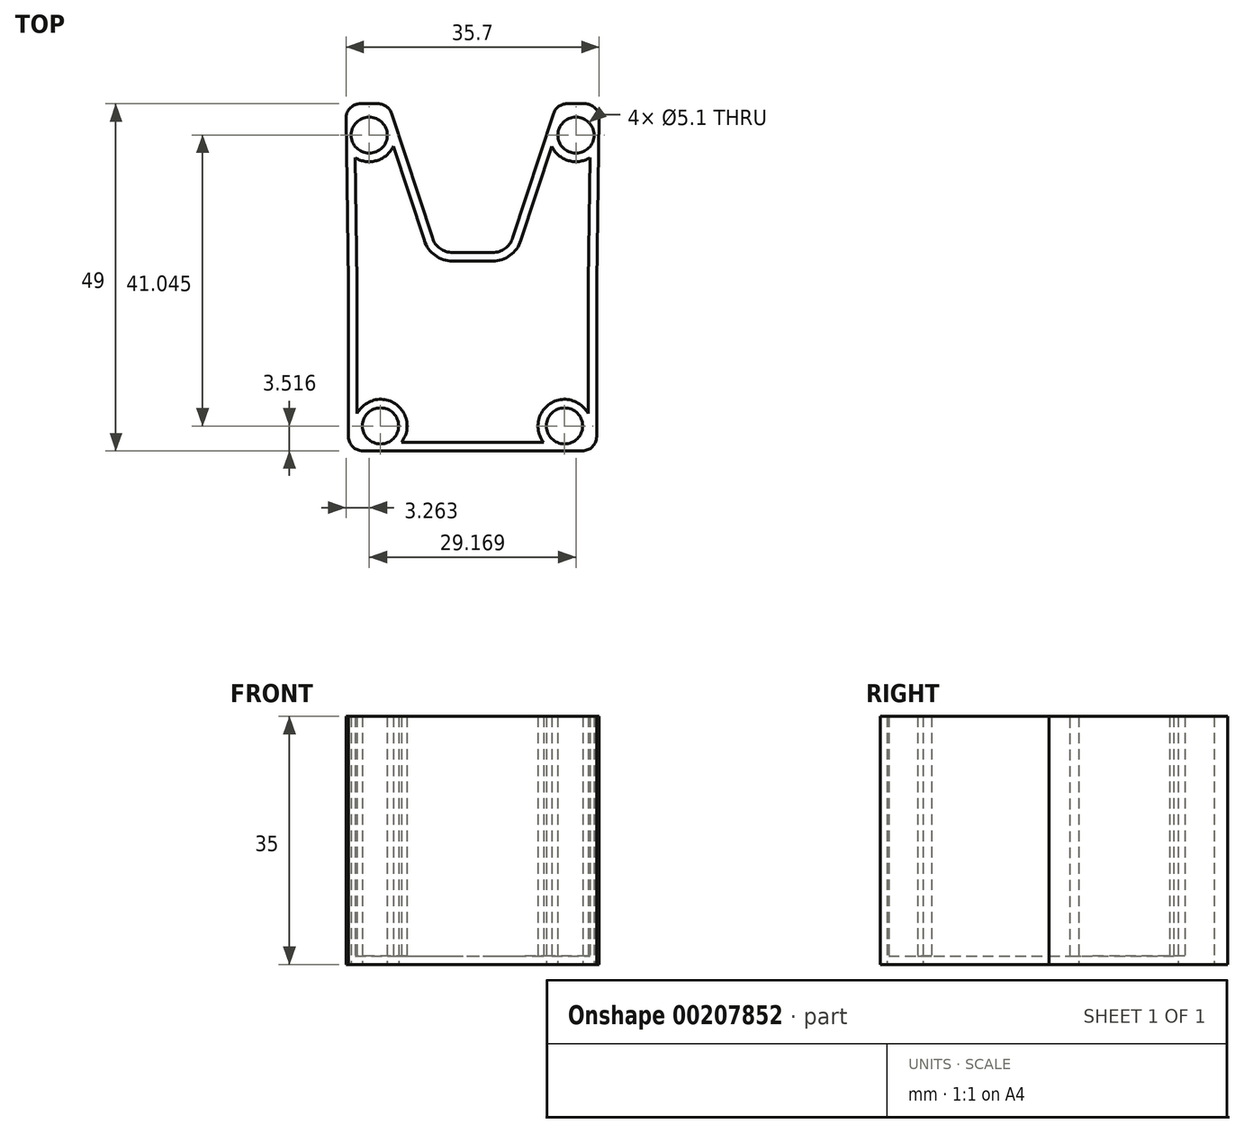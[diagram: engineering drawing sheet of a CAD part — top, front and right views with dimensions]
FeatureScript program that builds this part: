
annotation { "Feature Type Name" : "Feature", "Feature Type Description" : "" }
export const myFeature = defineFeature(function(context is Context, id is Id, definition is map)
    precondition{}
    {
        {
            var Q0;
            Q0=qCreatedBy(makeId("Top.planeOp"),FACE);
            var sketch = newSketch(context, id + "F0", { "sketchPlane" : qUnion([Q0])});
            skLineSegment(sketch, "E0.bottom", {"start": v(12.57, -4.38) * mm, "end": v(30.07, -4.38) * mm});
            skLineSegment(sketch, "E0.right", {"start": v(30.07, -2.38) * mm, "end": v(30.07, 19.44) * mm});
            skLineSegment(sketch, "E1", {"start": v(12.57, -4.38) * mm, "end": v(12.57, 23.62) * mm});
            skLineSegment(sketch, "E2", {"start": v(12.57, 23.62) * mm, "end": v(17.57, 23.62) * mm});
            skLineSegment(sketch, "E3", {"start": v(15.4, 23.62) * mm, "end": v(12.57, 23.62) * mm});
            skLineSegment(sketch, "E4.top", {"start": v(12.57, -4.38) * mm, "end": v(28.07, -4.38) * mm});
            skLineSegment(sketch, "E5", {"start": v(30.07, 19.44) * mm, "end": v(30.42, 42.59) * mm});
            skLineSegment(sketch, "E6", {"start": v(28.42, 44.62) * mm, "end": v(25.9, 44.62) * mm});
            skLineSegment(sketch, "E7", {"start": v(24, 43.24) * mm, "end": v(18.24, 25.68) * mm});
            skLineSegment(sketch, "E8.trimOffspring", {"start": v(24.45, 44.62) * mm, "end": v(30.45, 44.62) * mm});
            skLineSegment(sketch, "E9.trimOffspring", {"start": v(24.45, 44.62) * mm, "end": v(30.07, 44.62) * mm});
            skPoint(sketch, "E10.visualSharp", {"position": v(30.45, 44.62) * mm});
            skArc(sketch, "E10.filletArc", {"start": v(30.42, 42.59) * mm, "mid": v(29.84, 44.02) * mm, "end": v(28.42, 44.62) * mm});
            skPoint(sketch, "E11.visualSharp", {"position": v(24.45, 44.62) * mm});
            skArc(sketch, "E11.filletArc", {"start": v(25.9, 44.62) * mm, "mid": v(24.72, 44.24) * mm, "end": v(24, 43.24) * mm});
            skPoint(sketch, "E12.visualSharp", {"position": v(17.57, 23.62) * mm});
            skArc(sketch, "E12.filletArc", {"start": v(15.4, 23.62) * mm, "mid": v(17.15, 24.19) * mm, "end": v(18.24, 25.68) * mm});
            skArc(sketch, "E13.MirrorCS", {"start": v(-0.76, 44.62) * mm, "mid": v(0.4, 44.24) * mm, "end": v(1.14, 43.24) * mm});
            skLineSegment(sketch, "E14.MirrorCS", {"start": v(-3.28, 44.62) * mm, "end": v(-0.76, 44.62) * mm});
            skArc(sketch, "E15.MirrorCS", {"start": v(9.74, 23.62) * mm, "mid": v(7.98, 24.19) * mm, "end": v(6.9, 25.68) * mm});
            skLineSegment(sketch, "E16.MirrorCS", {"start": v(9.74, 23.62) * mm, "end": v(12.57, 23.62) * mm});
            skLineSegment(sketch, "E17.MirrorCS", {"start": v(12.57, 23.62) * mm, "end": v(7.57, 23.62) * mm});
            skLineSegment(sketch, "E18.MirrorCS", {"start": v(0.69, 44.62) * mm, "end": v(-5.31, 44.62) * mm});
            skLineSegment(sketch, "E19.MirrorCS", {"start": v(0.69, 44.62) * mm, "end": v(-4.93, 44.62) * mm});
            skArc(sketch, "E20.MirrorCS", {"start": v(-5.28, 42.59) * mm, "mid": v(-4.7, 44.02) * mm, "end": v(-3.28, 44.62) * mm});
            skLineSegment(sketch, "E21.MirrorCS", {"start": v(12.57, -4.38) * mm, "end": v(-2.93, -4.38) * mm});
            skPoint(sketch, "E22.MirrorP", {"position": v(-5.31, 44.62) * mm});
            skLineSegment(sketch, "E23.MirrorCS", {"start": v(1.14, 43.24) * mm, "end": v(6.9, 25.68) * mm});
            skPoint(sketch, "E24.MirrorP", {"position": v(7.57, 23.62) * mm});
            skLineSegment(sketch, "E25.MirrorCS", {"start": v(-4.93, 19.44) * mm, "end": v(-5.28, 42.59) * mm});
            skLineSegment(sketch, "E26.MirrorCS", {"start": v(-4.93, -2.38) * mm, "end": v(-4.93, 19.44) * mm});
            skPoint(sketch, "E27.MirrorP", {"position": v(0.69, 44.62) * mm});
            skPoint(sketch, "E28.orphan", {"position": v(-8.52, -4.38) * mm});
            skPoint(sketch, "E29.orphan", {"position": v(33.65, -4.38) * mm});
            skPoint(sketch, "E30.visualSharp", {"position": v(-4.93, -4.38) * mm});
            skArc(sketch, "E30.filletArc", {"start": v(-4.93, -2.38) * mm, "mid": v(-4.35, -3.8) * mm, "end": v(-2.93, -4.38) * mm});
            skPoint(sketch, "E31.visualSharp", {"position": v(30.07, -4.38) * mm});
            skArc(sketch, "E31.filletArc", {"start": v(28.07, -4.38) * mm, "mid": v(29.48, -3.8) * mm, "end": v(30.07, -2.38) * mm});
            skLineSegment(sketch, "E32", {"start": v(-4.93, -2.38) * mm, "end": v(-1.93, -2.38) * mm});
            skLineSegment(sketch, "E33", {"start": v(-1.93, -2.38) * mm, "end": v(-1.93, -4.38) * mm});
            skCircle(sketch, "E34", {"center": v(-0.42, -0.86) * mm, "radius": 1.5 * mm});
            skLineSegment(sketch, "E35", {"start": v(-1.93, -2.38) * mm, "end": v(-1.93, 2.04) * mm});
            skLineSegment(sketch, "E36", {"start": v(-1.93, -2.38) * mm, "end": v(2.26, -2.38) * mm});
            skLineSegment(sketch, "E37.MirrorCS", {"start": v(27.07, -2.38) * mm, "end": v(27.07, -4.38) * mm});
            skLineSegment(sketch, "E38.MirrorCS", {"start": v(30.07, -2.38) * mm, "end": v(27.07, -2.38) * mm});
            skLineSegment(sketch, "E39.MirrorCS", {"start": v(27.07, -2.38) * mm, "end": v(22.87, -2.38) * mm});
            skLineSegment(sketch, "E40.MirrorCS", {"start": v(27.07, -2.38) * mm, "end": v(27.07, 2.04) * mm});
            skCircle(sketch, "E41.MirrorC", {"center": v(25.55, -0.86) * mm, "radius": 1.5 * mm});
            skLineSegment(sketch, "E42", {"start": v(-3.28, 44.62) * mm, "end": v(-3.28, 42.62) * mm});
            skLineSegment(sketch, "E43", {"start": v(-5.28, 42.59) * mm, "end": v(-3.28, 42.62) * mm});
            skLineSegment(sketch, "E44", {"start": v(-2.02, 44.62) * mm, "end": v(-2.02, 40.12) * mm});
            skCircle(sketch, "E45", {"center": v(-2.02, 40.18) * mm, "radius": 1.5 * mm});
            skCircle(sketch, "E46.MirrorC", {"center": v(27.15, 40.18) * mm, "radius": 1.5 * mm});
            skLineSegment(sketch, "E47.bottom", {"start": v(20, 2.29) * mm, "end": v(5.14, 2.29) * mm});
            skLineSegment(sketch, "E47.top", {"start": v(20, 13.23) * mm, "end": v(5.14, 13.23) * mm});
            skLineSegment(sketch, "E47.left", {"start": v(20, 2.29) * mm, "end": v(20, 13.23) * mm});
            skLineSegment(sketch, "E47.right", {"start": v(5.14, 2.29) * mm, "end": v(5.14, 13.23) * mm});
            skPoint(sketch, "E47.middle", {"position": v(12.57, 7.76) * mm});
            skLineSegment(sketch, "E48.bottom", {"start": v(28.44, 3.6) * mm, "end": v(-3.3, 3.6) * mm});
            skLineSegment(sketch, "E48.top", {"start": v(28.44, 6.21) * mm, "end": v(-3.3, 6.21) * mm});
            skLineSegment(sketch, "E48.left", {"start": v(28.44, 3.6) * mm, "end": v(28.44, 6.21) * mm});
            skLineSegment(sketch, "E48.right", {"start": v(-3.3, 3.6) * mm, "end": v(-3.3, 6.21) * mm});
            skPoint(sketch, "E48.middle", {"position": v(12.57, 4.9) * mm});
            skCircle(sketch, "E49", {"center": v(-2.02, 40.18) * mm, "radius": 2.55 * mm});
            skCircle(sketch, "E50", {"center": v(27.15, 40.18) * mm, "radius": 2.55 * mm});
            skCircle(sketch, "E51", {"center": v(25.55, -0.86) * mm, "radius": 2.55 * mm});
            skCircle(sketch, "E52", {"center": v(-0.42, -0.86) * mm, "radius": 2.55 * mm});
            skSolve(sketch);
        }
        {
            var Q0;
            Q0 = qSketchRegion(id + "F0", true);
            var Q1;
            {var subQ0=sQuery(id+"F0.wireOp",EDGE,"E48.top");var subQ1=sQuery(id+"F0.wireOp",EDGE,"E1");var subQ2=makeQuery(id+"F0.imprint","INTERSECT",VERTEX,{"derivedFrom":[subQ1,subQ0]});Q1=makeQuery(id+"F0.imprint","IMPRINT",FACE,{"disambiguationData":[TD([[makeQuery(id+"F0.imprint","IMPRINT",EDGE,{"disambiguationData":[TD([[subQ2,-1.0]])],"derivedFrom":subQ1}),1.0]])]});}
            var Q2;
            {var subQ0=sQuery(id+"F0.wireOp",EDGE,"E48.top");var subQ1=sQuery(id+"F0.wireOp",EDGE,"E1");var subQ2=makeQuery(id+"F0.imprint","INTERSECT",VERTEX,{"derivedFrom":[subQ1,subQ0]});Q2=makeQuery(id+"F0.imprint","IMPRINT",FACE,{"disambiguationData":[TD([[makeQuery(id+"F0.imprint","IMPRINT",EDGE,{"disambiguationData":[TD([[subQ2,-1.0]])],"derivedFrom":subQ1}),-1.0]])]});}
            var Q3;
            {var subQ5=sQuery(id+"F0.wireOp",EDGE,"E48.left");Q3=makeQuery(id+"F0.imprint","IMPRINT",FACE,{"disambiguationData":[TD([[makeQuery(id+"F0.imprint","IMPRINT",EDGE,{"derivedFrom":subQ5}),1.0]])]});}
            var Q4;
            {var subQ0=sQuery(id+"F0.wireOp",EDGE,"E48.bottom");var subQ1=sQuery(id+"F0.wireOp",EDGE,"E1");var subQ2=makeQuery(id+"F0.imprint","INTERSECT",VERTEX,{"derivedFrom":[subQ1,subQ0]});Q4=makeQuery(id+"F0.imprint","IMPRINT",FACE,{"disambiguationData":[TD([[makeQuery(id+"F0.imprint","IMPRINT",EDGE,{"disambiguationData":[TD([[subQ2,-1.0]])],"derivedFrom":subQ1}),1.0]])]});}
            var Q5;
            {var subQ5=sQuery(id+"F0.wireOp",EDGE,"E48.right");Q5=makeQuery(id+"F0.imprint","IMPRINT",FACE,{"disambiguationData":[TD([[makeQuery(id+"F0.imprint","IMPRINT",EDGE,{"derivedFrom":subQ5}),-1.0]])]});}
            var Q6;
            {var subQ0=sQuery(id+"F0.wireOp",EDGE,"E47.bottom");var subQ1=sQuery(id+"F0.wireOp",EDGE,"E1");var subQ2=makeQuery(id+"F0.imprint","INTERSECT",VERTEX,{"derivedFrom":[subQ1,subQ0]});Q6=makeQuery(id+"F0.imprint","IMPRINT",FACE,{"disambiguationData":[TD([[makeQuery(id+"F0.imprint","IMPRINT",EDGE,{"disambiguationData":[TD([[subQ2,-1.0]])],"derivedFrom":subQ1}),1.0]])]});}
            var Q7;
            {var subQ0=sQuery(id+"F0.wireOp",EDGE,"E48.bottom");var subQ1=sQuery(id+"F0.wireOp",EDGE,"E1");var subQ2=makeQuery(id+"F0.imprint","INTERSECT",VERTEX,{"derivedFrom":[subQ1,subQ0]});Q7=makeQuery(id+"F0.imprint","IMPRINT",FACE,{"disambiguationData":[TD([[makeQuery(id+"F0.imprint","IMPRINT",EDGE,{"disambiguationData":[TD([[subQ2,-1.0]])],"derivedFrom":subQ1}),-1.0]])]});}
            var Q8;
            {var subQ0=sQuery(id+"F0.wireOp",EDGE,"E47.bottom");var subQ1=sQuery(id+"F0.wireOp",EDGE,"E1");var subQ2=makeQuery(id+"F0.imprint","INTERSECT",VERTEX,{"derivedFrom":[subQ1,subQ0]});Q8=makeQuery(id+"F0.imprint","IMPRINT",FACE,{"disambiguationData":[TD([[makeQuery(id+"F0.imprint","IMPRINT",EDGE,{"disambiguationData":[TD([[subQ2,-1.0]])],"derivedFrom":subQ1}),-1.0]])]});}
            extrude(context, id + "F1", {"entities" : qUnion([Q0, Q1, Q2, Q3, Q4, Q5, Q6, Q7, Q8]), "depth" : 35 * mm});
        }
        {
            var Q0;
            Q0=makeQuery(id+"F1.opExtrude","CAP_FACE",FACE,{"disambiguationData":[OSD([sQuery(id+"F0.wireOp",EDGE,"E0.right"),sQuery(id+"F0.wireOp",EDGE,"E3"),sQuery(id+"F0.wireOp",EDGE,"E4.top"),sQuery(id+"F0.wireOp",EDGE,"E5"),sQuery(id+"F0.wireOp",EDGE,"E7"),sQuery(id+"F0.wireOp",EDGE,"E9.trimOffspring"),sQuery(id+"F0.wireOp",EDGE,"E10.filletArc"),sQuery(id+"F0.wireOp",EDGE,"E11.filletArc"),sQuery(id+"F0.wireOp",EDGE,"E12.filletArc"),sQuery(id+"F0.wireOp",EDGE,"E13.MirrorCS"),sQuery(id+"F0.wireOp",EDGE,"E15.MirrorCS"),sQuery(id+"F0.wireOp",EDGE,"E17.MirrorCS"),sQuery(id+"F0.wireOp",EDGE,"E19.MirrorCS"),sQuery(id+"F0.wireOp",EDGE,"E20.MirrorCS"),sQuery(id+"F0.wireOp",EDGE,"E23.MirrorCS"),sQuery(id+"F0.wireOp",EDGE,"E25.MirrorCS"),sQuery(id+"F0.wireOp",EDGE,"E21.MirrorCS"),sQuery(id+"F0.wireOp",EDGE,"E26.MirrorCS"),sQuery(id+"F0.wireOp",EDGE,"E30.filletArc"),sQuery(id+"F0.wireOp",EDGE,"E31.filletArc"),sQuery(id+"F0.wireOp",EDGE,"E49"),sQuery(id+"F0.wireOp",EDGE,"E50"),sQuery(id+"F0.wireOp",EDGE,"E51"),sQuery(id+"F0.wireOp",EDGE,"E52")])],"isStart":false});
            shell(context, id + "F2", {"entities" : qUnion([Q0]), "thickness" : 1.2 * mm});
        }
    });
